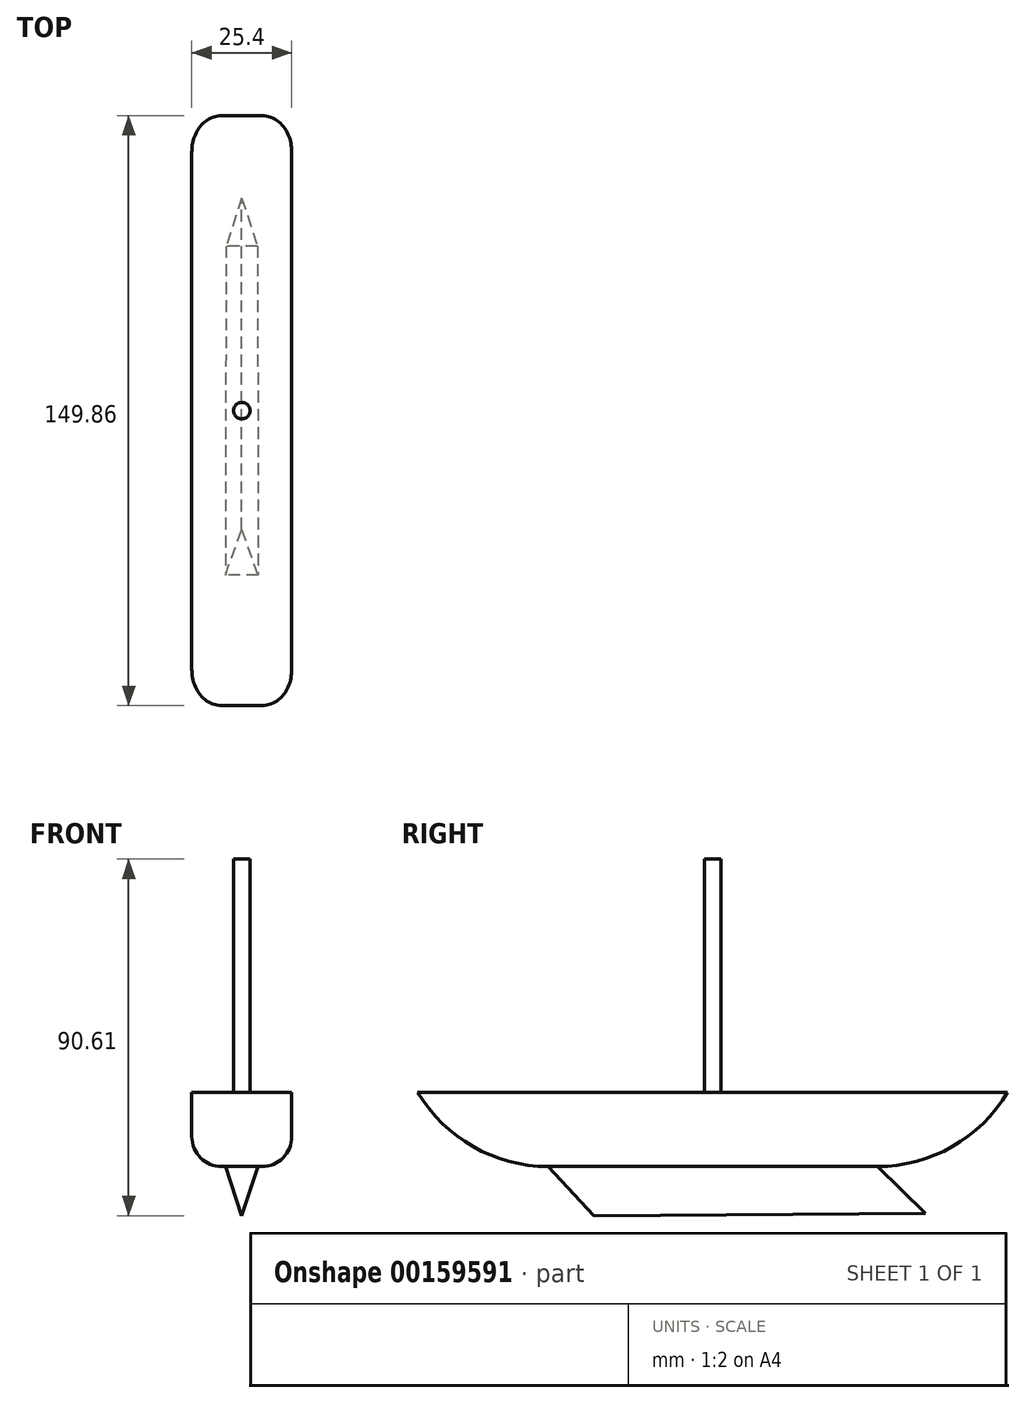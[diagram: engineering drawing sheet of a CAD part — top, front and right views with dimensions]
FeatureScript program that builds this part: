
annotation { "Feature Type Name" : "Feature", "Feature Type Description" : "" }
export const myFeature = defineFeature(function(context is Context, id is Id, definition is map)
    precondition{}
    {
        {
            var Q0;
            Q0=qCreatedBy(makeId("Right.planeOp"),FACE);
            var sketch = newSketch(context, id + "F0", { "sketchPlane" : qUnion([Q0])});
            skLineSegment(sketch, "E0.bottom", {"start": v(-41.82, 9.44) * mm, "end": v(41.82, 9.44) * mm});
            skLineSegment(sketch, "E0.top", {"start": v(-41.82, -9.44) * mm, "end": v(41.82, -9.44) * mm});
            skLineSegment(sketch, "E0.left", {"start": v(-41.82, 9.44) * mm, "end": v(-41.82, -9.44) * mm});
            skLineSegment(sketch, "E0.right", {"start": v(41.82, 9.44) * mm, "end": v(41.82, -9.44) * mm});
            skPoint(sketch, "E0.middle", {"position": v(0, 0) * mm});
            skLineSegment(sketch, "E1", {"start": v(-41.82, -9.44) * mm, "end": v(-74.93, 9.44) * mm});
            skLineSegment(sketch, "E2", {"start": v(-74.93, 9.44) * mm, "end": v(-41.82, 9.44) * mm});
            skLineSegment(sketch, "E3", {"start": v(41.82, -9.44) * mm, "end": v(74.93, 9.44) * mm});
            skLineSegment(sketch, "E4", {"start": v(74.93, 9.44) * mm, "end": v(41.82, 9.44) * mm});
            skArc(sketch, "E5", {"start": v(41.82, -9.44) * mm, "mid": v(60.88, -4.39) * mm, "end": v(74.93, 9.44) * mm});
            skArc(sketch, "E6", {"start": v(-74.93, 9.44) * mm, "mid": v(-60.88, -4.39) * mm, "end": v(-41.82, -9.44) * mm});
            skLineSegment(sketch, "E7", {"start": v(-41.82, -9.44) * mm, "end": v(-30.2, -21.93) * mm});
            skLineSegment(sketch, "E8", {"start": v(41.82, -9.44) * mm, "end": v(54.02, -21.35) * mm});
            skLineSegment(sketch, "E9", {"start": v(54.02, -21.35) * mm, "end": v(-30.2, -21.93) * mm});
            skSolve(sketch);
        }
        {
            var Q0;
            Q0=makeQuery(id+"F0.imprint","IMPRINT",FACE,{"disambiguationData":[TD([[makeQuery(id+"F0.imprint","IMPRINT",EDGE,{"derivedFrom":sQuery(id+"F0.wireOp",EDGE,"E1")}),1.0]])]});
            var Q1;
            Q1=makeQuery(id+"F0.imprint","IMPRINT",FACE,{"disambiguationData":[TD([[makeQuery(id+"F0.imprint","IMPRINT",EDGE,{"derivedFrom":sQuery(id+"F0.wireOp",EDGE,"E3")}),-1.0]])]});
            var Q2;
            Q2=makeQuery(id+"F0.imprint","IMPRINT",FACE,{"disambiguationData":[TD([[makeQuery(id+"F0.imprint","IMPRINT",EDGE,{"derivedFrom":sQuery(id+"F0.wireOp",EDGE,"E0.right")}),1.0]])]});
            var Q3;
            Q3=makeQuery(id+"F0.imprint","IMPRINT",FACE,{"disambiguationData":[TD([[makeQuery(id+"F0.imprint","IMPRINT",EDGE,{"derivedFrom":sQuery(id+"F0.wireOp",EDGE,"E0.bottom")}),-1.0]])]});
            var Q4;
            Q4=makeQuery(id+"F0.imprint","IMPRINT",FACE,{"disambiguationData":[TD([[makeQuery(id+"F0.imprint","IMPRINT",EDGE,{"derivedFrom":sQuery(id+"F0.wireOp",EDGE,"E0.left")}),-1.0]])]});
            var Q5;
            Q5=sQuery(id+"F0.wireOp",EDGE,"E6");
            var Q6;
            Q6=sQuery(id+"F0.wireOp",EDGE,"E0.top");
            var Q7;
            Q7=sQuery(id+"F0.wireOp",EDGE,"E5");
            var Q8;
            Q8=sQuery(id+"F0.wireOp",EDGE,"E4");
            var Q9;
            Q9=sQuery(id+"F0.wireOp",EDGE,"E0.bottom");
            var Q10;
            Q10=sQuery(id+"F0.wireOp",EDGE,"E2");
            extrude(context, id + "F1", {"entities" : qUnion([Q0, Q1, Q2, Q3, Q4]), "surfaceEntities" : qUnion([Q5, Q6, Q7, Q8, Q9, Q10]), "endBound" : BoundingType.SYMMETRIC, "depth" : 25.4 * mm});
        }
        {
            var Q0;
            Q0=makeQuery(id+"F0.imprint","IMPRINT",FACE,{"disambiguationData":[TD([[makeQuery(id+"F0.imprint","IMPRINT",EDGE,{"derivedFrom":sQuery(id+"F0.wireOp",EDGE,"E0.top")}),-1.0]])]});
            extrude(context, id + "F2", {"entities" : qUnion([Q0]), "operationType" : NewBodyOperationType.ADD, "endBound" : BoundingType.SYMMETRIC, "depth" : 12.7 * mm});
        }
        {
            var Q0;
            Q0=makeQuery(id+"F2.opExtrude","CAP_EDGE",EDGE,{"disambiguationData":[OSD([sQuery(id+"F0.wireOp",EDGE,"E9")])],"isStart":true});
            chamfer(context, id + "F3", {"entities" : qUnion([Q0]), "chamferType" : ChamferType.TWO_OFFSETS, "width1" : 19.05 * mm, "oppositeDirection" : false, "width2" : 6.35 * mm, "tangentPropagation" : true});
        }
        {
            var Q0;
            Q0=makeQuery(id+"F2.opExtrude","CAP_EDGE",EDGE,{"disambiguationData":[OSD([sQuery(id+"F0.wireOp",EDGE,"E9")])],"isStart":false});
            chamfer(context, id + "F4", {"entities" : qUnion([Q0]), "chamferType" : ChamferType.TWO_OFFSETS, "width1" : 6.35 * mm, "oppositeDirection" : false, "width2" : 19.05 * mm, "tangentPropagation" : true});
        }
        {
            var Q0;
            Q0=makeQuery(id+"F1.opExtrude","CAP_EDGE",EDGE,{"disambiguationData":[OSD([sQuery(id+"F0.wireOp",EDGE,"E5")])],"isStart":true});
            var Q1;
            Q1=makeQuery(id+"F1.opExtrude","CAP_EDGE",EDGE,{"disambiguationData":[OSD([sQuery(id+"F0.wireOp",EDGE,"E0.top")])],"isStart":true});
            var Q2;
            Q2=makeQuery(id+"F1.opExtrude","CAP_EDGE",EDGE,{"disambiguationData":[OSD([sQuery(id+"F0.wireOp",EDGE,"E6")])],"isStart":true});
            fillet(context, id + "F5", {"entities" : qUnion([Q0, Q1, Q2]), "radius" : 7.62 * mm, "tangentPropagation" : true, "allowEdgeOverflow" : false});
        }
        {
            var Q0;
            Q0=makeQuery(id+"F1.opExtrude","CAP_EDGE",EDGE,{"disambiguationData":[OSD([sQuery(id+"F0.wireOp",EDGE,"E6")])],"isStart":false});
            var Q1;
            Q1=makeQuery(id+"F1.opExtrude","CAP_EDGE",EDGE,{"disambiguationData":[OSD([sQuery(id+"F0.wireOp",EDGE,"E0.top")])],"isStart":false});
            var Q2;
            Q2=makeQuery(id+"F1.opExtrude","CAP_EDGE",EDGE,{"disambiguationData":[OSD([sQuery(id+"F0.wireOp",EDGE,"E5")])],"isStart":false});
            fillet(context, id + "F6", {"entities" : qUnion([Q0, Q1, Q2]), "radius" : 7.62 * mm, "tangentPropagation" : true, "allowEdgeOverflow" : false});
        }
        {
            var Q0;
            Q0=qCreatedBy(makeId("Right.planeOp"),FACE);
            var sketch = newSketch(context, id + "F7", { "sketchPlane" : qUnion([Q0])});
            skLineSegment(sketch, "E10", {"start": v(0, 0) * mm, "end": v(0, 68.68) * mm});
            skLineSegment(sketch, "E11", {"start": v(0, 68.68) * mm, "end": v(2.1, 68.68) * mm});
            skLineSegment(sketch, "E12", {"start": v(2.1, 68.68) * mm, "end": v(2.1, 0) * mm});
            skLineSegment(sketch, "E13", {"start": v(2.1, 0) * mm, "end": v(0, 0) * mm});
            skSolve(sketch);
        }
        {
            var Q0;
            Q0 = qSketchRegion(id + "F7", true);
            var Q1;
            Q1=sQuery(id+"F7.wireOp",EDGE,"Vo5gDxHt-pM4L-qwJ2-DdXp-003RQYl8BxN7");
            var Q2;
            Q2=sQuery(id+"F7.wireOp",EDGE,"E10");
            revolve(context, id + "F8", {"operationType" : NewBodyOperationType.ADD, "entities" : qUnion([Q0]), "surfaceEntities" : qUnion([Q1]), "axis" : qUnion([Q2]), "revolveType" : RevolveType.FULL, "oppositeDirection" : true});
        }
    });
